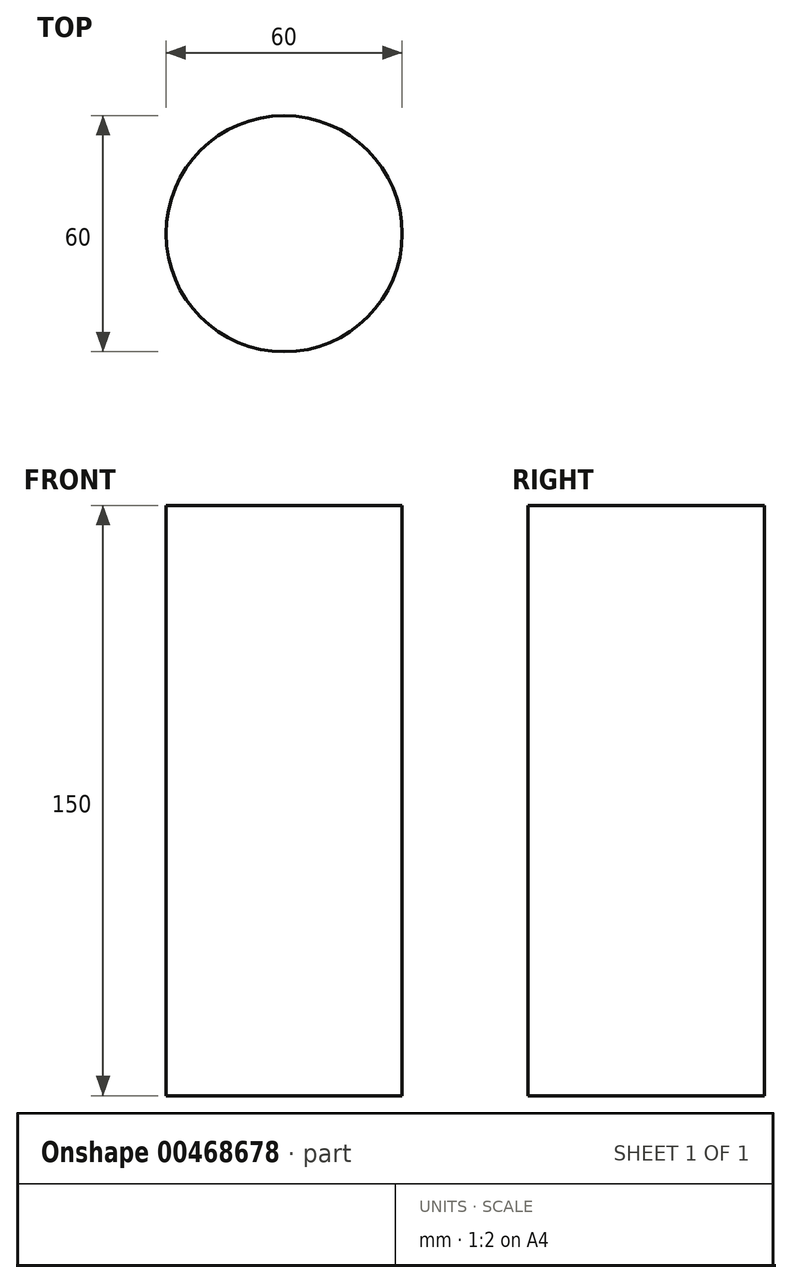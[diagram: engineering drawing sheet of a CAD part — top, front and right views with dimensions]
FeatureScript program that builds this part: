
annotation { "Feature Type Name" : "Feature", "Feature Type Description" : "" }
export const myFeature = defineFeature(function(context is Context, id is Id, definition is map)
    precondition{}
    {
        {
            var Q0;
            Q0=qCreatedBy(makeId("Top.planeOp"),FACE);
            var sketch = newSketch(context, id + "F0", { "sketchPlane" : qUnion([Q0])});
            skCircle(sketch, "E0", {"center": v(0, 0) * mm, "radius": 30 * mm});
            skSolve(sketch);
        }
        {
            var Q0;
            Q0 = qSketchRegion(id + "F0", true);
            extrude(context, id + "F1", {"entities" : qUnion([Q0]), "endBound" : BoundingType.SYMMETRIC, "depth" : 150 * mm});
        }
    });
